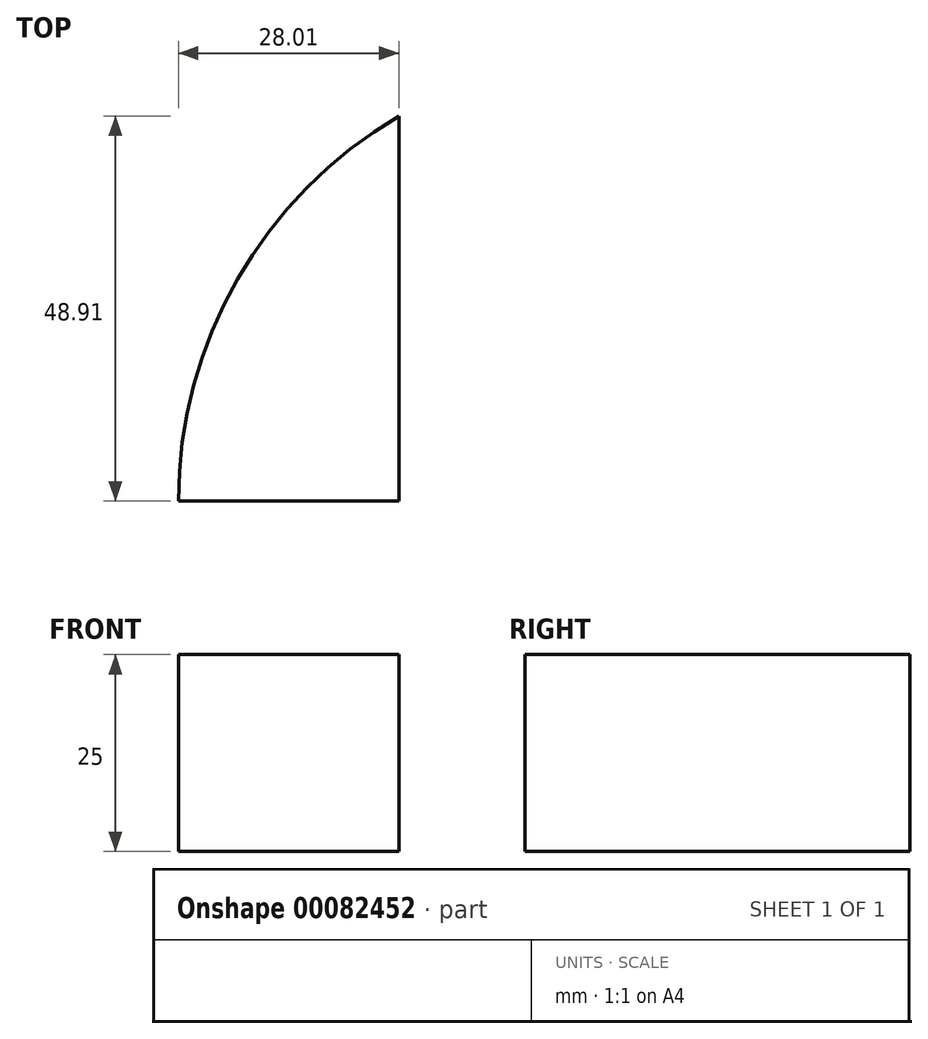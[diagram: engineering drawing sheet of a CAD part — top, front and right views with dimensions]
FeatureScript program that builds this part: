
annotation { "Feature Type Name" : "Feature", "Feature Type Description" : "" }
export const myFeature = defineFeature(function(context is Context, id is Id, definition is map)
    precondition{}
    {
        {
            var Q0;
            Q0=qCreatedBy(makeId("Top.planeOp"),FACE);
            var sketch = newSketch(context, id + "F0", { "sketchPlane" : qUnion([Q0])});
            skLineSegment(sketch, "E0.bottom", {"start": v(-68.21, 0) * mm, "end": v(5.24, 0) * mm});
            skLineSegment(sketch, "E0.top", {"start": v(-68.21, 48.9) * mm, "end": v(5.24, 48.9) * mm});
            skLineSegment(sketch, "E0.left", {"start": v(-68.21, 0) * mm, "end": v(-68.21, 48.9) * mm});
            skLineSegment(sketch, "E0.right", {"start": v(5.24, 0) * mm, "end": v(5.24, 48.9) * mm});
            skSolve(sketch);
        }
        {
            var Q0;
            Q0 = qSketchRegion(id + "F0", true);
            extrude(context, id + "F1", {"entities" : qUnion([Q0]), "depth" : 25 * mm});
        }
        {
            var Q0;
            Q0=makeQuery(id+"F1.opExtrude","SWEPT_FACE",FACE,{"disambiguationData":[OSD([sQuery(id+"F0.wireOp",EDGE,"E0.bottom")])]});
            var sketch = newSketch(context, id + "F2", { "sketchPlane" : qUnion([Q0])});
            skLineSegment(sketch, "E1", {"start": v(33.94, 31.82) * mm, "end": v(33.94, -9.54) * mm});
            skSolve(sketch);
        }
        {
            var Q0;
            Q0=makeQuery(id+"F1.opExtrude","SWEPT_FACE",FACE,{"disambiguationData":[OSD([sQuery(id+"F0.wireOp",EDGE,"E0.right")])]});
            var Q1;
            Q1=sQuery(id+"F2.wireOp",EDGE,"E1");
            revolve(context, id + "F3", {"operationType" : NewBodyOperationType.INTERSECT, "entities" : qUnion([Q0]), "axis" : qUnion([Q1]), "revolveType" : RevolveType.FULL});
        }
    });
